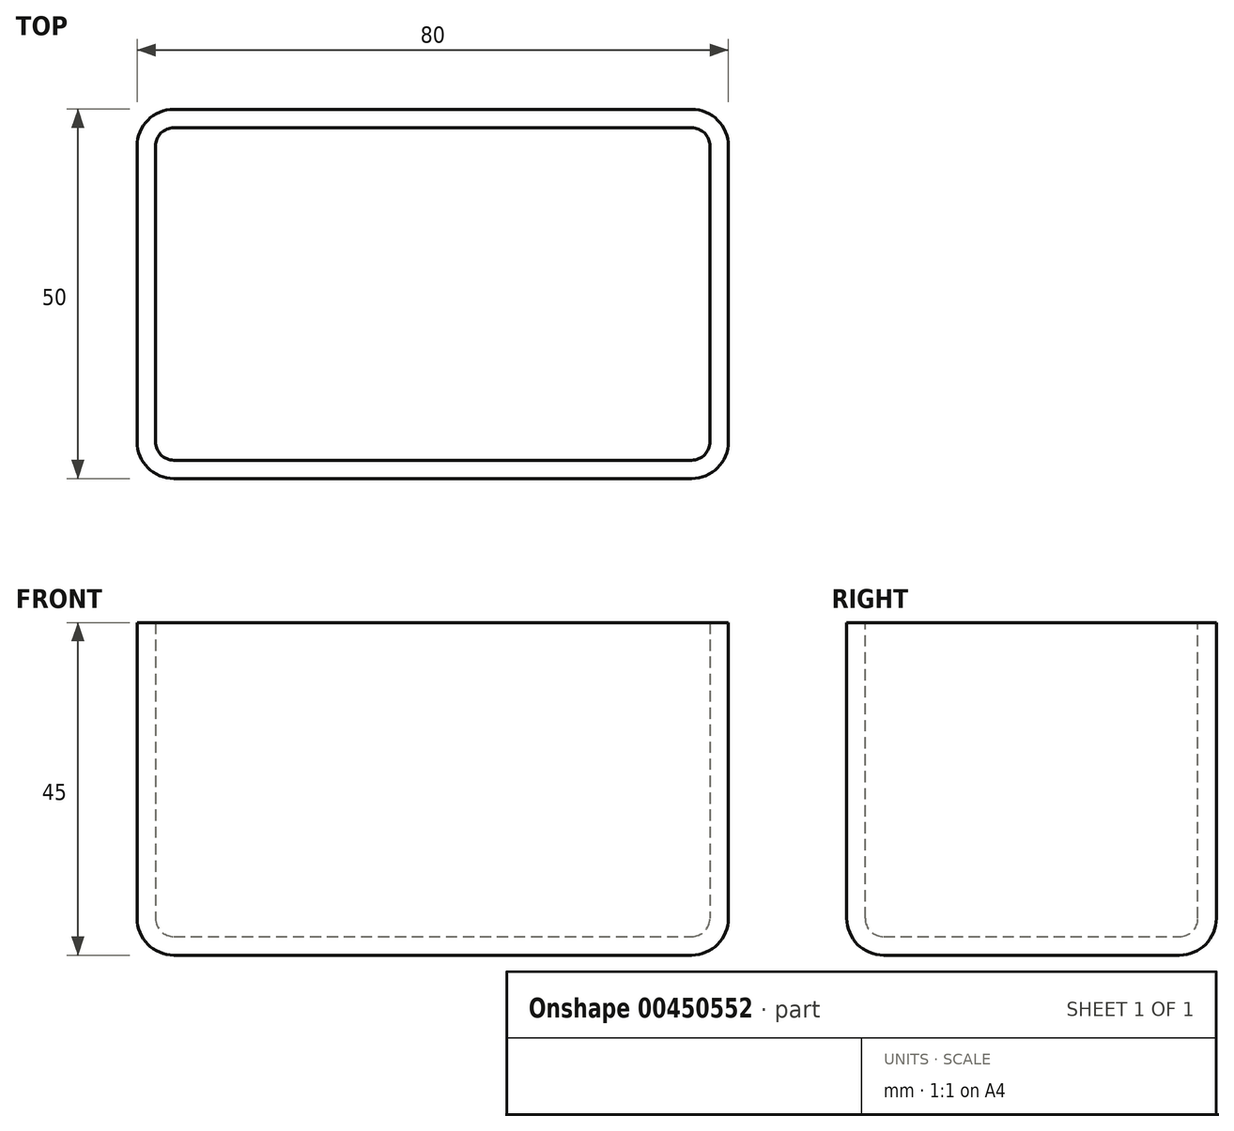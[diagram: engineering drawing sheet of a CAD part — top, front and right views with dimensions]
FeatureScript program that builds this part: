
annotation { "Feature Type Name" : "Feature", "Feature Type Description" : "" }
export const myFeature = defineFeature(function(context is Context, id is Id, definition is map)
    precondition{}
    {
        {
            var Q0;
            Q0=qCreatedBy(makeId("Top.planeOp"),FACE);
            var sketch = newSketch(context, id + "F0", { "sketchPlane" : qUnion([Q0])});
            skLineSegment(sketch, "E0.bottom", {"start": v(-33.22, 32.4) * mm, "end": v(46.78, 32.4) * mm});
            skLineSegment(sketch, "E0.top", {"start": v(-33.22, -17.6) * mm, "end": v(46.78, -17.6) * mm});
            skLineSegment(sketch, "E0.left", {"start": v(-33.22, 32.4) * mm, "end": v(-33.22, -17.6) * mm});
            skLineSegment(sketch, "E0.right", {"start": v(46.78, 32.4) * mm, "end": v(46.78, -17.6) * mm});
            skSolve(sketch);
        }
        {
            var Q0;
            Q0=makeQuery(id+"F0.imprint","IMPRINT",FACE,{"disambiguationData":[TD([[makeQuery(id+"F0.imprint","IMPRINT",EDGE,{"derivedFrom":sQuery(id+"F0.wireOp",EDGE,"E0.bottom")}),-1.0]])]});
            extrude(context, id + "F1", {"entities" : qUnion([Q0]), "depth" : 45 * mm});
        }
        {
            var Q0;
            Q0=makeQuery(id+"F1.opExtrude","SWEPT_EDGE",EDGE,{"disambiguationData":[OSD([sQuery(id+"F0.wireOp",EDGE,"E0.top"),sQuery(id+"F0.wireOp",EDGE,"E0.left")])]});
            var Q1;
            Q1=makeQuery(id+"F1.opExtrude","SWEPT_EDGE",EDGE,{"disambiguationData":[OSD([sQuery(id+"F0.wireOp",EDGE,"E0.top"),sQuery(id+"F0.wireOp",EDGE,"E0.right")])]});
            var Q2;
            Q2=makeQuery(id+"F1.opExtrude","SWEPT_EDGE",EDGE,{"disambiguationData":[OSD([sQuery(id+"F0.wireOp",EDGE,"E0.bottom"),sQuery(id+"F0.wireOp",EDGE,"E0.right")])]});
            var Q3;
            Q3=makeQuery(id+"F1.opExtrude","SWEPT_EDGE",EDGE,{"disambiguationData":[OSD([sQuery(id+"F0.wireOp",EDGE,"E0.bottom"),sQuery(id+"F0.wireOp",EDGE,"E0.left")])]});
            var Q4;
            Q4=makeQuery(id+"F1.opExtrude","CAP_FACE",FACE,{"disambiguationData":[OSD([sQuery(id+"F0.wireOp",EDGE,"E0.bottom"),sQuery(id+"F0.wireOp",EDGE,"E0.top"),sQuery(id+"F0.wireOp",EDGE,"E0.left"),sQuery(id+"F0.wireOp",EDGE,"E0.right")])],"isStart":true});
            fillet(context, id + "F2", {"entities" : qUnion([Q0, Q1, Q2, Q3, Q4]), "radius" : 5 * mm, "tangentPropagation" : true, "allowEdgeOverflow" : false});
        }
        {
            var Q0;
            Q0=makeQuery(id+"F1.opExtrude","CAP_FACE",FACE,{"disambiguationData":[OSD([sQuery(id+"F0.wireOp",EDGE,"E0.bottom"),sQuery(id+"F0.wireOp",EDGE,"E0.top"),sQuery(id+"F0.wireOp",EDGE,"E0.left"),sQuery(id+"F0.wireOp",EDGE,"E0.right")])],"isStart":false});
            shell(context, id + "F3", {"entities" : qUnion([Q0]), "thickness" : 2.5 * mm});
        }
    });
